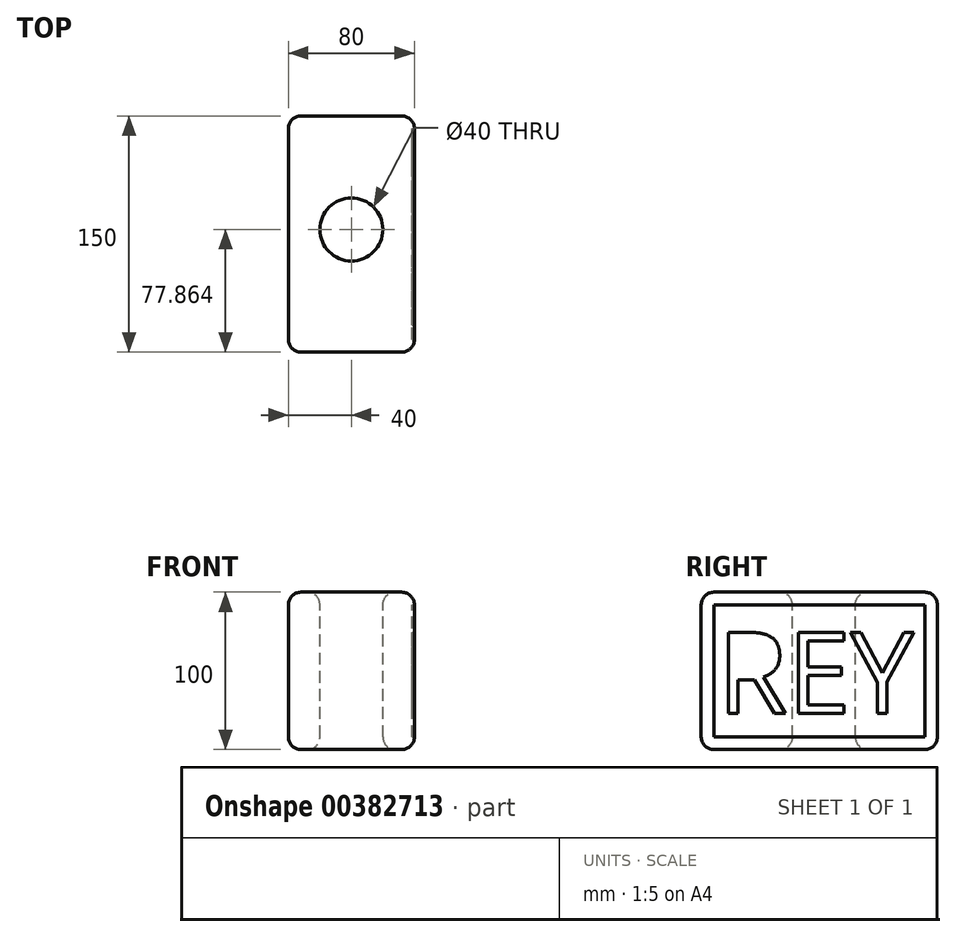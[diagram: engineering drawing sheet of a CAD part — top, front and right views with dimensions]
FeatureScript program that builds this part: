
annotation { "Feature Type Name" : "Feature", "Feature Type Description" : "" }
export const myFeature = defineFeature(function(context is Context, id is Id, definition is map)
    precondition{}
    {
        {
            var Q0;
            Q0=qCreatedBy(makeId("Front.planeOp"),FACE);
            var sketch = newSketch(context, id + "F0", { "sketchPlane" : qUnion([Q0])});
            skLineSegment(sketch, "E0.bottom", {"start": v(40, -50) * mm, "end": v(-40, -50) * mm});
            skLineSegment(sketch, "E0.top", {"start": v(40, 50) * mm, "end": v(-40, 50) * mm});
            skLineSegment(sketch, "E0.left", {"start": v(40, -50) * mm, "end": v(40, 50) * mm});
            skLineSegment(sketch, "E0.right", {"start": v(-40, -50) * mm, "end": v(-40, 50) * mm});
            skPoint(sketch, "E0.middle", {"position": v(0, 0) * mm});
            skSolve(sketch);
        }
        {
            var Q0;
            Q0 = qSketchRegion(id + "F0", true);
            extrude(context, id + "F1", {"entities" : qUnion([Q0]), "depth" : 150 * mm});
        }
        {
            var Q0;
            Q0=makeQuery(id+"F1.opExtrude","SWEPT_FACE",FACE,{"disambiguationData":[OSD([sQuery(id+"F0.wireOp",EDGE,"E0.top")])]});
            var sketch = newSketch(context, id + "F2", { "sketchPlane" : qUnion([Q0])});
            skCircle(sketch, "E1", {"center": v(0, -72.14) * mm, "radius": 20 * mm});
            skSolve(sketch);
        }
        {
            var Q0;
            Q0=makeQuery(id+"F2.imprint","IMPRINT",FACE,{"disambiguationData":[TD([[makeQuery(id+"F2.imprint","IMPRINT",EDGE,{"derivedFrom":sQuery(id+"F2.wireOp",EDGE,"E1")}),1.0]])]});
            var Q1;
            Q1=sQuery(id+"F2.wireOp",EDGE,"E1");
            extrude(context, id + "F3", {"entities" : qUnion([Q0]), "operationType" : NewBodyOperationType.REMOVE, "surfaceEntities" : qUnion([Q1]), "endBound" : BoundingType.SYMMETRIC, "oppositeDirection" : true, "depth" : 283.8 * mm});
        }
        {
            var Q0;
            Q0=makeQuery(id+"F1.opExtrude","SWEPT_FACE",FACE,{"disambiguationData":[OSD([sQuery(id+"F0.wireOp",EDGE,"E0.top")])]});
            var Q1;
            Q1=makeQuery(id+"F1.opExtrude","CAP_FACE",FACE,{"disambiguationData":[OSD([sQuery(id+"F0.wireOp",EDGE,"E0.bottom"),sQuery(id+"F0.wireOp",EDGE,"E0.top"),sQuery(id+"F0.wireOp",EDGE,"E0.left"),sQuery(id+"F0.wireOp",EDGE,"E0.right")])],"isStart":false});
            var Q2;
            Q2=makeQuery(id+"F1.opExtrude","SWEPT_FACE",FACE,{"disambiguationData":[OSD([sQuery(id+"F0.wireOp",EDGE,"E0.left")])]});
            var Q3;
            Q3=makeQuery(id+"F1.opExtrude","SWEPT_FACE",FACE,{"disambiguationData":[OSD([sQuery(id+"F0.wireOp",EDGE,"E0.bottom")])]});
            var Q4;
            Q4=makeQuery(id+"F1.opExtrude","SWEPT_FACE",FACE,{"disambiguationData":[OSD([sQuery(id+"F0.wireOp",EDGE,"E0.right")])]});
            var Q5;
            Q5=makeQuery(id+"F1.opExtrude","CAP_FACE",FACE,{"disambiguationData":[OSD([sQuery(id+"F0.wireOp",EDGE,"E0.bottom"),sQuery(id+"F0.wireOp",EDGE,"E0.top"),sQuery(id+"F0.wireOp",EDGE,"E0.left"),sQuery(id+"F0.wireOp",EDGE,"E0.right")])],"isStart":true});
            fillet(context, id + "F4", {"entities" : qUnion([Q0, Q1, Q2, Q3, Q4, Q5]), "radius" : 8 * mm, "tangentPropagation" : true, "allowEdgeOverflow" : false});
        }
        {
            var Q0;
            Q0=makeQuery(id+"F1.opExtrude","SWEPT_FACE",FACE,{"disambiguationData":[OSD([sQuery(id+"F0.wireOp",EDGE,"E0.left")])]});
            var sketch = newSketch(context, id + "F5", { "sketchPlane" : qUnion([Q0])});
            skLineSegment(sketch, "E2.bottom", {"start": v(-142, 42) * mm, "end": v(-8, 42) * mm});
            skLineSegment(sketch, "E2.top", {"start": v(-142, -42) * mm, "end": v(-8, -42) * mm});
            skLineSegment(sketch, "E2.left", {"start": v(-142, 42) * mm, "end": v(-142, -42) * mm});
            skLineSegment(sketch, "E2.right", {"start": v(-8, 42) * mm, "end": v(-8, -42) * mm});
            skText(sketch, "E3", { "text": "REY", "fontName": "OpenSans-Regular.ttf"});
            const initialGuessF5  = {"E3": [-0.13983, -0.02704, 1, 0, 0.0519]};
            skSetInitialGuess(sketch, initialGuessF5);
            skSolve(sketch);
        }
        {
            var Q0;
            Q0 = qSketchRegion(id + "F5", true);
            extrude(context, id + "F6", {"entities" : qUnion([Q0]), "operationType" : NewBodyOperationType.REMOVE, "oppositeDirection" : true, "depth" : 1.6 * mm});
        }
    });
